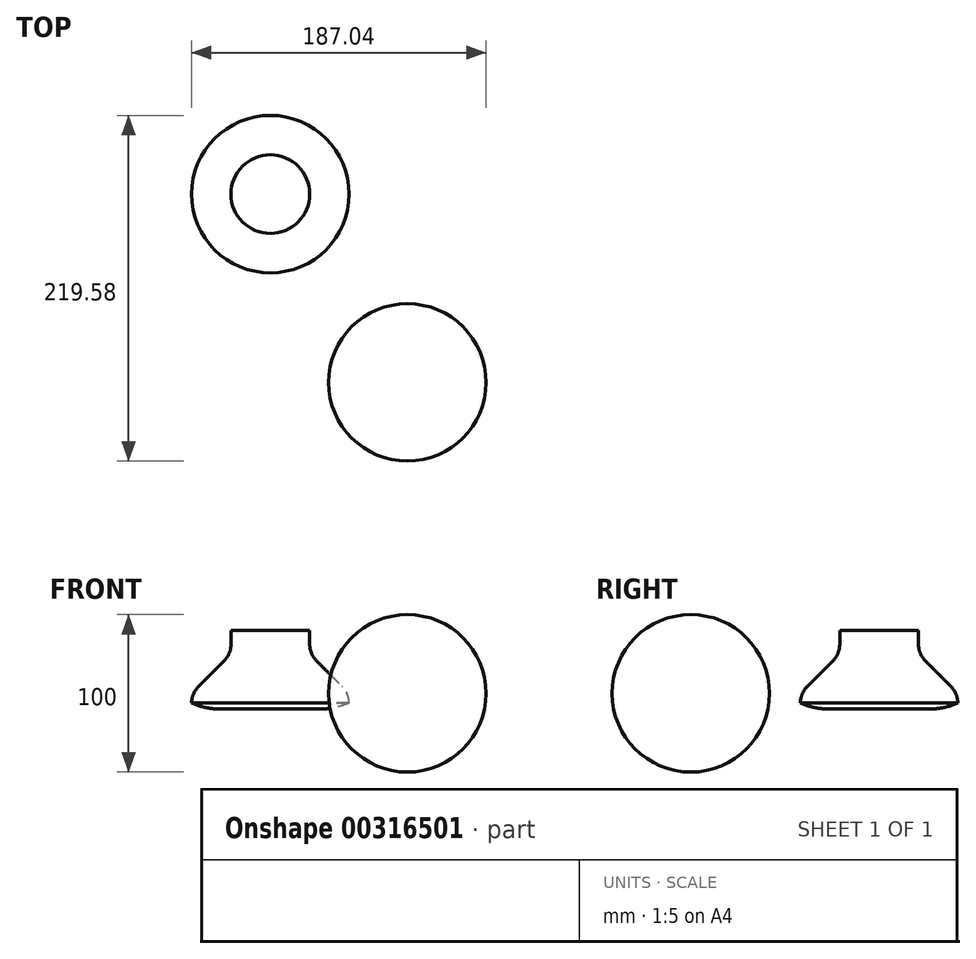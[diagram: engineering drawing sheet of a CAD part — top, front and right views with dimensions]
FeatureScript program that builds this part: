
annotation { "Feature Type Name" : "Feature", "Feature Type Description" : "" }
export const myFeature = defineFeature(function(context is Context, id is Id, definition is map)
    precondition{}
    {
        {
            var Q0;
            Q0=qCreatedBy(makeId("Front.planeOp"),FACE);
            var sketch = newSketch(context, id + "F0", { "sketchPlane" : qUnion([Q0])});
            skCircle(sketch, "E0", {"center": v(0, 0) * mm, "radius": 50 * mm});
            skSolve(sketch);
        }
        {
            var Q0;
            Q0=makeQuery(id+"F0.imprint","IMPRINT",FACE,{"disambiguationData":[TD([[makeQuery(id+"F0.imprint","IMPRINT",EDGE,{"derivedFrom":sQuery(id+"F0.wireOp",EDGE,"E0")}),1.0]])]});
            extrude(context, id + "F1", {"entities" : qUnion([Q0]), "depth" : 100 * mm});
        }
        {
            var Q0;
            Q0=makeQuery(id+"F1.opExtrude","CAP_EDGE",EDGE,{"disambiguationData":[OSD([sQuery(id+"F0.wireOp",EDGE,"E0")])],"isStart":false});
            var Q1;
            Q1=makeQuery(id+"F1.opExtrude","CAP_EDGE",EDGE,{"disambiguationData":[OSD([sQuery(id+"F0.wireOp",EDGE,"E0")])],"isStart":true});
            fillet(context, id + "F2", {"entities" : qUnion([Q0, Q1]), "radius" : 50 * mm, "tangentPropagation" : true, "allowEdgeOverflow" : false});
        }
        {
            var Q0;
            Q0=qCreatedBy(makeId("Top.planeOp"),FACE);
            var sketch = newSketch(context, id + "F3", { "sketchPlane" : qUnion([Q0])});
            skCircle(sketch, "E1", {"center": v(-87.04, 69.58) * mm, "radius": 50 * mm});
            skSolve(sketch);
        }
        {
            var Q0;
            Q0=makeQuery(id+"F3.imprint","IMPRINT",FACE,{"disambiguationData":[TD([[makeQuery(id+"F3.imprint","IMPRINT",EDGE,{"derivedFrom":sQuery(id+"F3.wireOp",EDGE,"E1")}),1.0]])]});
            extrude(context, id + "F4", {"entities" : qUnion([Q0]), "depth" : 25 * mm});
        }
        {
            var Q0;
            Q0=makeQuery(id+"F4.opExtrude","CAP_EDGE",EDGE,{"disambiguationData":[OSD([sQuery(id+"F3.wireOp",EDGE,"E1")])],"isStart":false});
            chamfer(context, id + "F5", {"entities" : qUnion([Q0]), "width" : 25 * mm, "tangentPropagation" : true});
        }
        {
            var Q0;
            Q0=makeQuery(id+"F4.opExtrude","CAP_FACE",FACE,{"disambiguationData":[OSD([sQuery(id+"F3.wireOp",EDGE,"E1")])],"isStart":false});
            extrude(context, id + "F6", {"entities" : qUnion([Q0]), "operationType" : NewBodyOperationType.ADD, "depth" : 15 * mm});
        }
        {
            var Q0;
            Q0=makeQuery(id+"F4.opExtrude","CAP_FACE",FACE,{"disambiguationData":[OSD([sQuery(id+"F3.wireOp",EDGE,"E1")])],"isStart":true});
            extrude(context, id + "F7", {"entities" : qUnion([Q0]), "operationType" : NewBodyOperationType.ADD, "depth" : 10 * mm});
        }
        {
            var Q0;
            Q0=makeQuery(id+"F5.opChamfer","BLEND_FACE",FACE,{"disambiguationData":[OSD([sQuery(id+"F3.wireOp",EDGE,"E1")])]});
            fillet(context, id + "F8", {"entities" : qUnion([Q0]), "tangentPropagation" : true, "radius" : 15 * mm, "defaultsChanged" : true, "vertexSettings" : [], "allowEdgeOverflow" : false});
        }
        {
            var Q0;
            Q0=makeQuery(id+"F7.opExtrude","CAP_EDGE",EDGE,{"disambiguationData":[OSD([sQuery(id+"F3.wireOp",EDGE,"E1")])],"isStart":false});
            fillet(context, id + "F9", {"entities" : qUnion([Q0]), "tangentPropagation" : true, "radius" : 50 * mm, "defaultsChanged" : true, "vertexSettings" : [], "allowEdgeOverflow" : false});
        }
    });
